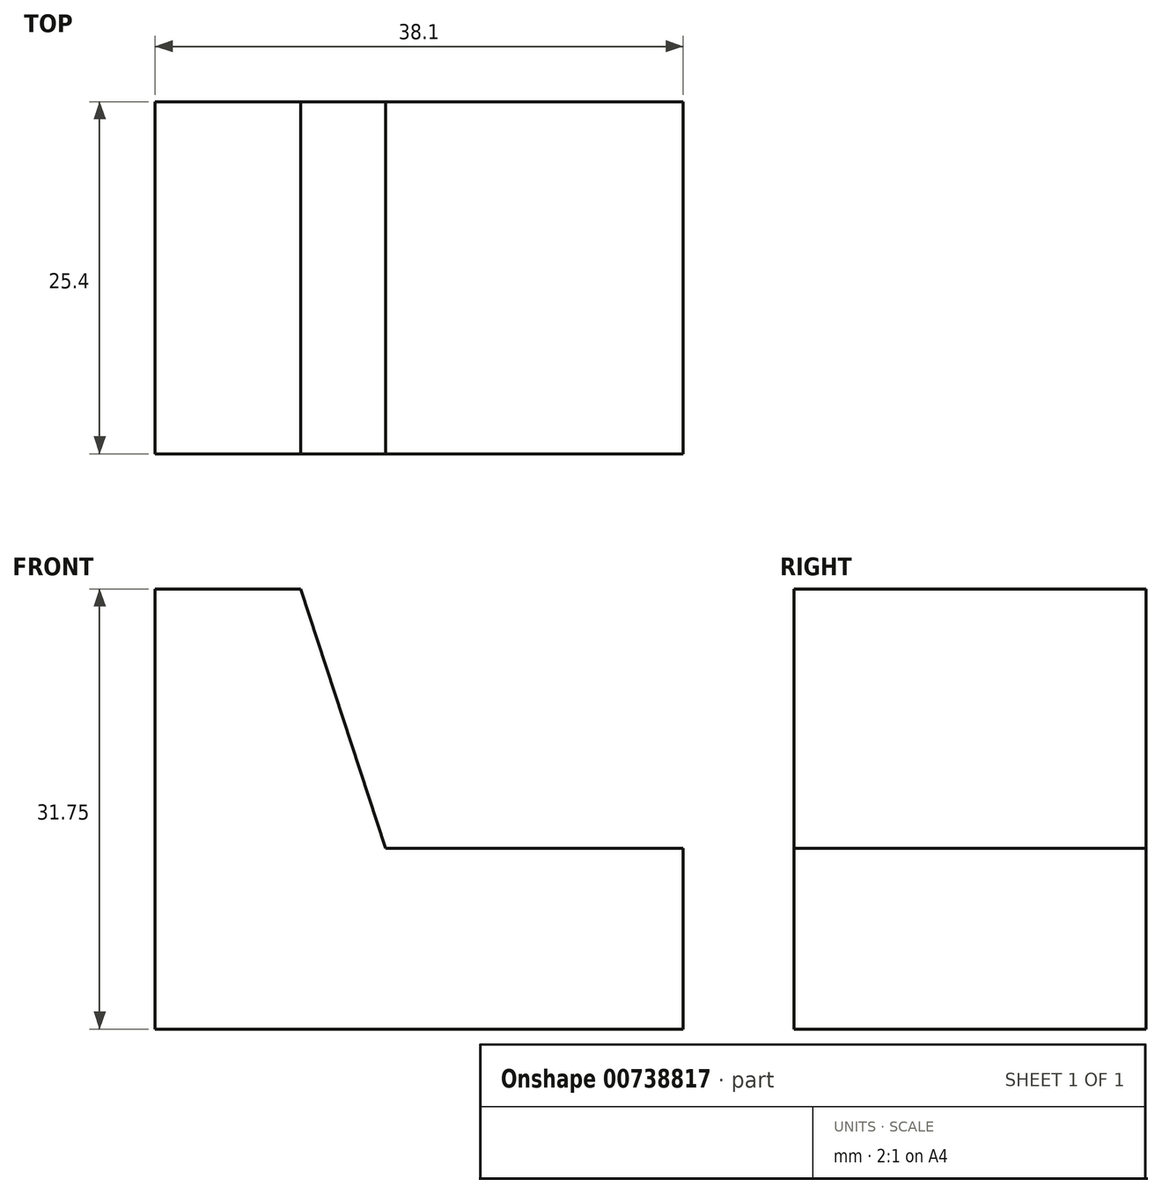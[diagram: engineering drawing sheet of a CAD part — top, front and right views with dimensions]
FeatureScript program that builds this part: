
annotation { "Feature Type Name" : "Feature", "Feature Type Description" : "" }
export const myFeature = defineFeature(function(context is Context, id is Id, definition is map)
    precondition{}
    {
        {
            var Q0;
            Q0=qCreatedBy(makeId("Front.planeOp"),FACE);
            var sketch = newSketch(context, id + "F0", { "sketchPlane" : qUnion([Q0])});
            skLineSegment(sketch, "E0", {"start": v(0, 0) * mm, "end": v(0, 31.75) * mm});
            skLineSegment(sketch, "E1", {"start": v(0, 31.75) * mm, "end": v(38.1, 31.75) * mm});
            skLineSegment(sketch, "E2", {"start": v(38.1, 31.75) * mm, "end": v(38.1, 0) * mm});
            skLineSegment(sketch, "E3", {"start": v(38.1, 0) * mm, "end": v(0, 0) * mm});
            skSolve(sketch);
        }
        {
            var Q0;
            Q0 = qSketchRegion(id + "F0", true);
            extrude(context, id + "F1", {"entities" : qUnion([Q0]), "depth" : 25.4 * mm, "offsetDistance" : 25.4 * mm});
        }
        {
            var Q0;
            Q0=makeQuery(id+"F1.opExtrude","CAP_FACE",FACE,{"disambiguationData":[OSD([sQuery(id+"F0.wireOp",EDGE,"E0"),sQuery(id+"F0.wireOp",EDGE,"E1"),sQuery(id+"F0.wireOp",EDGE,"E2"),sQuery(id+"F0.wireOp",EDGE,"E3")])],"isStart":false});
            var sketch = newSketch(context, id + "F2", { "sketchPlane" : qUnion([Q0])});
            skLineSegment(sketch, "E4", {"start": v(21.02, 31.75) * mm, "end": v(25.4, 18.36) * mm});
            skLineSegment(sketch, "E5", {"start": v(25.4, 18.36) * mm, "end": v(38.1, 18.36) * mm});
            skSolve(sketch);
        }
        {
            var Q0;
            {var subQ0=sQuery(id+"F2.wireOp",EDGE,"E4");Q0=makeQuery(id+"F2.imprint","IMPRINT",FACE,{"disambiguationData":[TD([[makeQuery(id+"F2.imprint","IMPRINT",EDGE,{"derivedFrom":subQ0}),1.0]])]});}
            extrude(context, id + "F3", {"entities" : qUnion([Q0]), "operationType" : NewBodyOperationType.REMOVE, "oppositeDirection" : true, "depth" : 25.4 * mm, "offsetDistance" : 25.4 * mm});
        }
        {
            var Q0;
            Q0=makeQuery(id+"F1.opExtrude","CAP_FACE",FACE,{"disambiguationData":[OSD([sQuery(id+"F0.wireOp",EDGE,"E0"),sQuery(id+"F0.wireOp",EDGE,"E1"),sQuery(id+"F0.wireOp",EDGE,"E2"),sQuery(id+"F0.wireOp",EDGE,"E3")])],"isStart":false});
            var sketch = newSketch(context, id + "F4", { "sketchPlane" : qUnion([Q0])});
            skLineSegment(sketch, "E6", {"start": v(10.51, 31.75) * mm, "end": v(16.63, 13.05) * mm});
            skLineSegment(sketch, "E7", {"start": v(16.63, 13.05) * mm, "end": v(38.1, 13.05) * mm});
            skSolve(sketch);
        }
        {
            var Q0;
            {var subQ3=sQuery(id+"F4.wireOp",EDGE,"E6");Q0=makeQuery(id+"F4.imprint","IMPRINT",FACE,{"disambiguationData":[TD([[makeQuery(id+"F4.imprint","IMPRINT",EDGE,{"derivedFrom":subQ3}),1.0]])]});}
            extrude(context, id + "F5", {"entities" : qUnion([Q0]), "operationType" : NewBodyOperationType.REMOVE, "endBound" : BoundingType.THROUGH_ALL, "oppositeDirection" : true, "depth" : 25.4 * mm, "offsetDistance" : 25.4 * mm});
        }
    });
